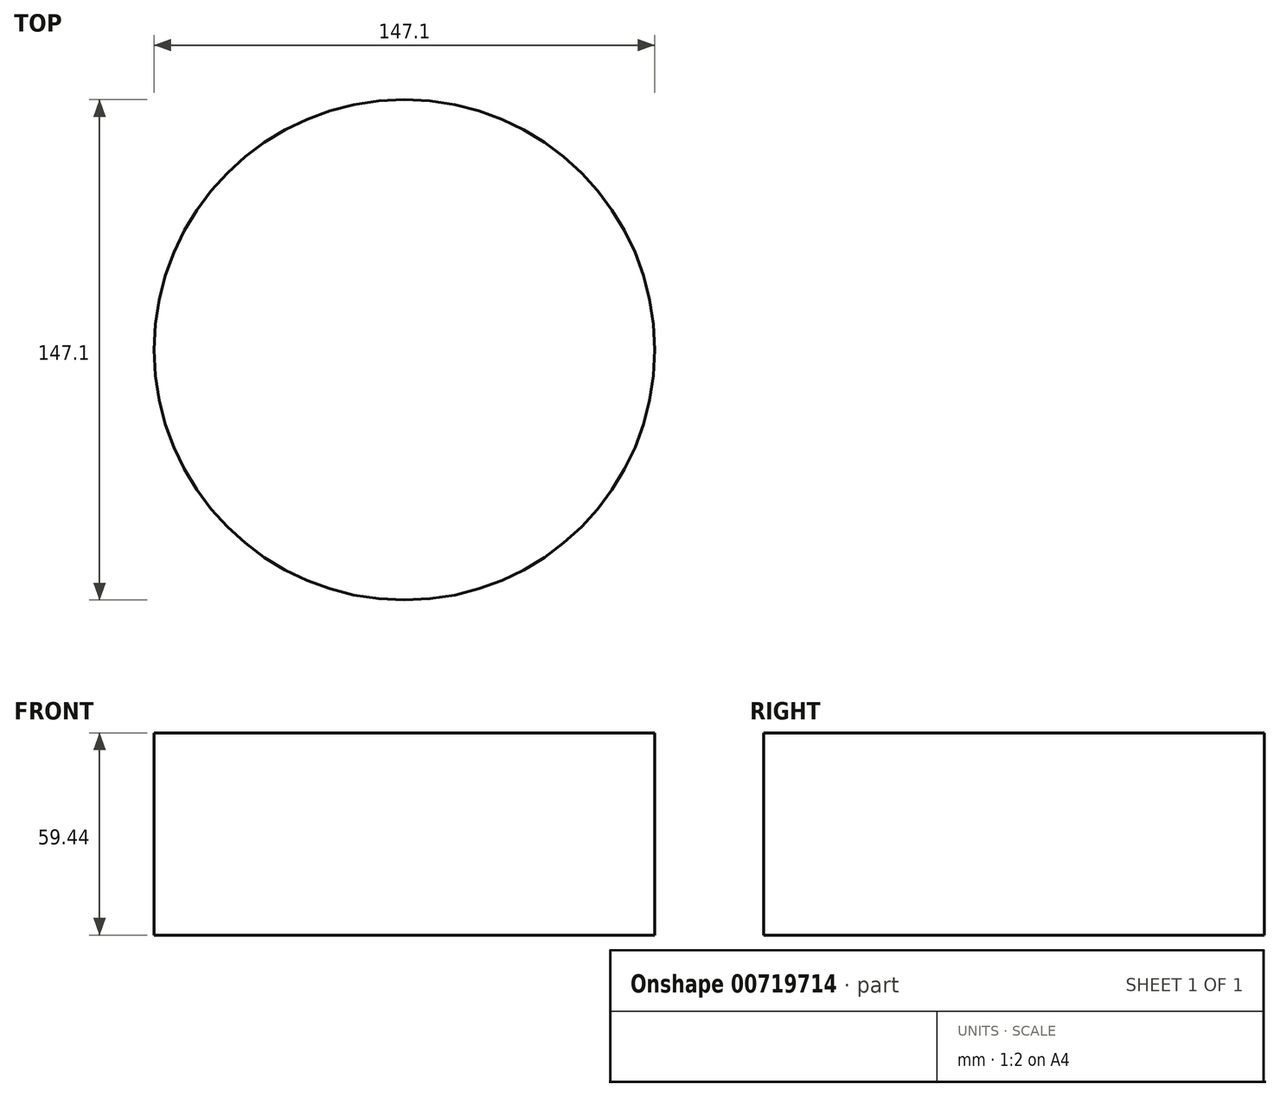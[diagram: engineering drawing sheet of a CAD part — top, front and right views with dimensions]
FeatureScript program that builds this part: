
annotation { "Feature Type Name" : "Feature", "Feature Type Description" : "" }
export const myFeature = defineFeature(function(context is Context, id is Id, definition is map)
    precondition{}
    {
        {
            var Q0;
            Q0=qCreatedBy(makeId("Top.planeOp"),FACE);
            var sketch = newSketch(context, id + "F0", { "sketchPlane" : qUnion([Q0])});
            skCircle(sketch, "E0", {"center": v(0, 0) * mm, "radius": 73.55 * mm});
            skSolve(sketch);
        }
        {
            var Q0;
            Q0=makeQuery(id+"F0.imprint","IMPRINT",FACE,{"disambiguationData":[TD([[makeQuery(id+"F0.imprint","IMPRINT",EDGE,{"derivedFrom":sQuery(id+"F0.wireOp",EDGE,"E0")}),1.0]])]});
            extrude(context, id + "F1", {"entities" : qUnion([Q0]), "depth" : 59.44 * mm, "offsetDistance" : 25.4 * mm});
        }
    });
